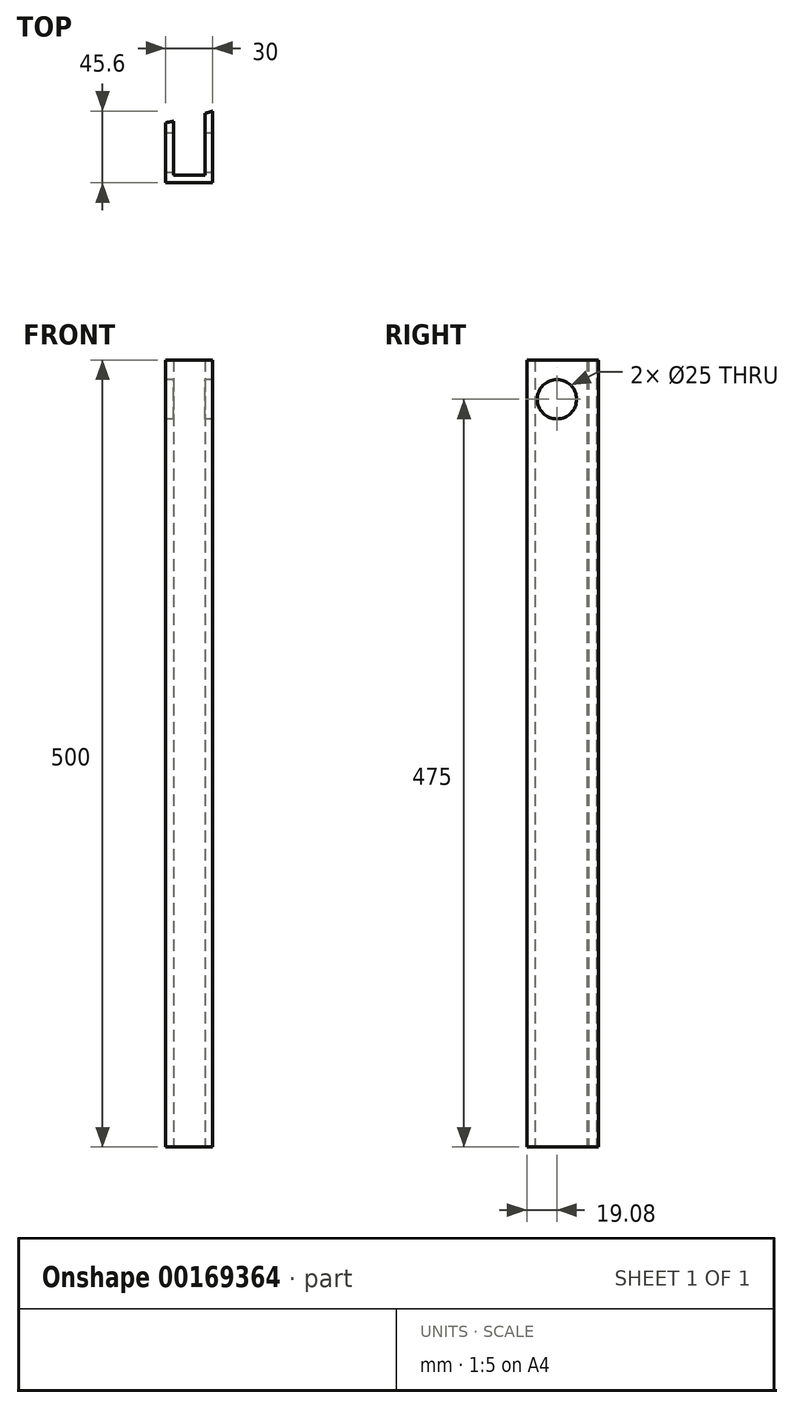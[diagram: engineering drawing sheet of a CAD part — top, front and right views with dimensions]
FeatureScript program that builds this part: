
annotation { "Feature Type Name" : "Feature", "Feature Type Description" : "" }
export const myFeature = defineFeature(function(context is Context, id is Id, definition is map)
    precondition{}
    {
        {
            var Q0;
            Q0=qCreatedBy(makeId("Top.planeOp"),FACE);
            var sketch = newSketch(context, id + "F0", { "sketchPlane" : qUnion([Q0])});
            skPoint(sketch, "E0", {"position": v(15, 21.57) * mm});
            skPoint(sketch, "E1", {"position": v(15, -16.6) * mm});
            skPoint(sketch, "E2", {"position": v(-15, -16.6) * mm});
            skPoint(sketch, "E3", {"position": v(-15, 29) * mm});
            skLineSegment(sketch, "E4", {"start": v(15, 21.57) * mm, "end": v(15, -16.6) * mm});
            skLineSegment(sketch, "E5", {"start": v(-15, -16.6) * mm, "end": v(-15, 29) * mm});
            skArc(sketch, "E6", {"start": v(-15, 29) * mm, "mid": v(-0.1, 24.85) * mm, "end": v(15, 21.57) * mm});
            skLineSegment(sketch, "E7", {"start": v(-15, -16.6) * mm, "end": v(15, -16.6) * mm});
            skPoint(sketch, "E8", {"position": v(-10, -16.6) * mm});
            skPoint(sketch, "E9", {"position": v(10, -16.6) * mm});
            skLineSegment(sketch, "E10", {"start": v(-10, -16.6) * mm, "end": v(-10, 27.5) * mm});
            skLineSegment(sketch, "E11", {"start": v(10, -16.6) * mm, "end": v(10, 22.56) * mm});
            skLineSegment(sketch, "E12", {"start": v(-10, 27.5) * mm, "end": v(10, 22.56) * mm});
            skPoint(sketch, "E13", {"position": v(-10, -11.6) * mm});
            skPoint(sketch, "E14", {"position": v(10, -11.6) * mm});
            skLineSegment(sketch, "E15", {"start": v(-10, -11.6) * mm, "end": v(10, -11.6) * mm});
            skSolve(sketch);
        }
        {
            var Q0;
            {var subQ4=sQuery(id+"F0.wireOp",EDGE,"E5");Q0=makeQuery(id+"F0.imprint","IMPRINT",FACE,{"disambiguationData":[TD([[makeQuery(id+"F0.imprint","IMPRINT",EDGE,{"derivedFrom":subQ4}),-1.0]])]});}
            var Q1;
            {var subQ5=sQuery(id+"F0.wireOp",EDGE,"E15");Q1=makeQuery(id+"F0.imprint","IMPRINT",FACE,{"disambiguationData":[TD([[makeQuery(id+"F0.imprint","IMPRINT",EDGE,{"derivedFrom":subQ5}),-1.0]])]});}
            var Q2;
            {var subQ4=sQuery(id+"F0.wireOp",EDGE,"E4");Q2=makeQuery(id+"F0.imprint","IMPRINT",FACE,{"disambiguationData":[TD([[makeQuery(id+"F0.imprint","IMPRINT",EDGE,{"derivedFrom":subQ4}),-1.0]])]});}
            extrude(context, id + "F1", {"entities" : qUnion([Q0, Q1, Q2]), "depth" : 500 * mm});
        }
        {
            var Q0;
            Q0=makeQuery(id+"F1.opExtrude","SWEPT_FACE",FACE,{"disambiguationData":[OSD([sQuery(id+"F0.wireOp",EDGE,"E4")])]});
            var sketch = newSketch(context, id + "F2", { "sketchPlane" : qUnion([Q0])});
            skPoint(sketch, "E16", {"position": v(-16.6, 500) * mm});
            skPoint(sketch, "E17", {"position": v(21.57, 500) * mm});
            skPoint(sketch, "E18", {"position": v(2.5, 500) * mm});
            skCircle(sketch, "E19", {"center": v(2.5, 475) * mm, "radius": 12.5 * mm});
            skSolve(sketch);
        }
        {
            var Q0;
            Q0=makeQuery(id+"F2.imprint","IMPRINT",FACE,{"disambiguationData":[TD([[makeQuery(id+"F2.imprint","IMPRINT",EDGE,{"derivedFrom":sQuery(id+"F2.wireOp",EDGE,"E19")}),1.0]])]});
            extrude(context, id + "F3", {"entities" : qUnion([Q0]), "operationType" : NewBodyOperationType.REMOVE, "oppositeDirection" : true, "depth" : 50 * mm});
        }
        {
            var Q0;
            Q0=makeQuery(id+"F1.opExtrude","SWEPT_BODY",BODY,{"disambiguationData":[OSD([sQuery(id+"F0.wireOp",EDGE,"E4"),sQuery(id+"F0.wireOp",EDGE,"E5"),sQuery(id+"F0.wireOp",EDGE,"E6"),sQuery(id+"F0.wireOp",EDGE,"E7"),sQuery(id+"F0.wireOp",EDGE,"E10"),sQuery(id+"F0.wireOp",EDGE,"E11"),sQuery(id+"F0.wireOp",EDGE,"E15")])]});
            var Q1;
            Q1=qCreatedBy(makeId("Right.planeOp"),FACE);
            mirror(context, id + "F4", {"entities" : qUnion([Q0]), "mirrorPlane" : qUnion([Q1])});
        }
        {
            var Q0;
            Q0=makeQuery(id+"F1.opExtrude","SWEPT_BODY",BODY,{"disambiguationData":[OSD([sQuery(id+"F0.wireOp",EDGE,"E4"),sQuery(id+"F0.wireOp",EDGE,"E5"),sQuery(id+"F0.wireOp",EDGE,"E6"),sQuery(id+"F0.wireOp",EDGE,"E7"),sQuery(id+"F0.wireOp",EDGE,"E10"),sQuery(id+"F0.wireOp",EDGE,"E11"),sQuery(id+"F0.wireOp",EDGE,"E15")])]});
            deleteBodies(context, id + "F5", {"entities" : qUnion([Q0])});
        }
    });
